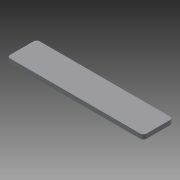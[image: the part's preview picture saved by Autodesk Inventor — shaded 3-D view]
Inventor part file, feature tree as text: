
AUTODESK INVENTOR PART (.ipt)
format: ipt  version: 2013 (Build 170138000, 138)  size: 74,752 bytes
history: native  units: in
note: dims shown in document units (in); Inventor stores cm internally (conversion verified against a paired STEP export)
features: extrude x1, sketch x1
ambient origin geometry x8: Origin, YZ Plane, XZ Plane, XY Plane, X Axis, Y Axis, Z Axis, Center Point
bodies: Solid1 (feature_tree)
feature tree (2):
  extrude  "Extrusion1"  Depth=5.0in
  sketch  "Sketch1"  dims[d0=23.0in d1=5.0in d2=0.5in d3=0.75in d4=0.0in]
